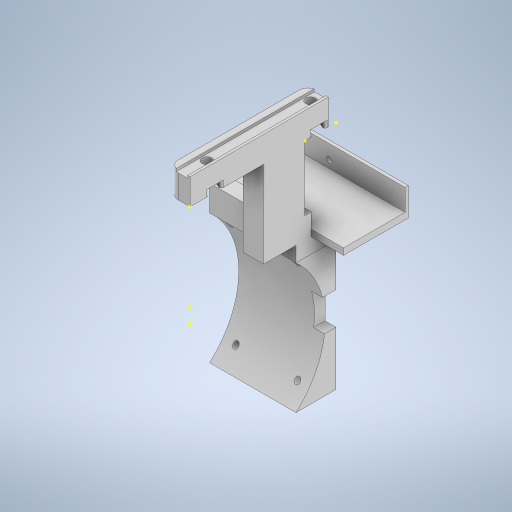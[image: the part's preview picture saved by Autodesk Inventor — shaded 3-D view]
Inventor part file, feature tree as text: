
AUTODESK INVENTOR PART (.ipt)
format: ipt  version: 2024 (Build 280153000, 153)  size: 507,392 bytes
history: native  units: in
note: dims shown in document units (in); Inventor stores cm internally (conversion verified against a paired STEP export)
features: sketch x26, extrude x18, projected_geometry x4, fillet x2, sweep x1
ambient origin geometry x8: Origin, YZ Plane, XZ Plane, XY Plane, X Axis, Y Axis, Z Axis, Center Point
bodies: Solid1 (feature_tree), Solid2 (feature_tree)
feature tree (51):
  extrude  "Extrusion1"  Depth=2.5197in
  extrude  "Extrusion2"  Depth=1.8898in
  extrude  "Extrusion3"  Depth=0.4724in TaperAngle=0.0deg
  fillet  "Fillet1"  Radius=0.0433in
  fillet  "Fillet2"  Radius=0.2126in
  extrude  "Extrusion19"  Depth=0.4724in TaperAngle=0.0deg
  extrude  "Extrusion21"  Depth=0.1181in TaperAngle=0.0deg
  sketch  "Sketch41"  dims[d17=0.1772in d18=0.0394in]
  extrude  "Extrusion22"  Depth=0.0394in
  extrude  "Extrusion25"  Depth=0.4724in
  sweep  "Sweep4"
  extrude  "Extrusion26"  Depth=0.1181in
  sketch  "Sketch60"  dims[d136=0.2756in d137=1.5748in]
  extrude  "Extrusion27"  Depth=0.3937in TaperAngle=0.0deg
  sketch  "Sketch62"  dims[d154=4.1063in d155=0.0in d164=2.3622in]
  extrude  "Extrusion28"  TaperAngle=180.0deg  [1 undecoded]
  sketch  "Sketch64"  dims[d168=2.4813in d169=0.0in d170=1.5748in d171=0.0in]
  extrude  "Extrusion29"  Depth=1.5748in
  sketch  "Sketch66"  dims[d179=0.5906in d180=0.1969in]
  sketch  "Sketch67"  dims[d181=0.5906in d182=0.8248in d183=0.0in]
  extrude  "Extrusion30"  Depth=0.2756in TaperAngle=0.0deg
  extrude  "Extrusion31"  Depth=2.3622in
  extrude  "Extrusion32"  TaperAngle=0.0deg  [1 undecoded]
  extrude  "Extrusion33"  Depth=1.5748in TaperAngle=0.0deg
  extrude  "Extrusion34"  Depth=1.5748in TaperAngle=0.0deg
  extrude  "Extrusion35"  Depth=0.1969in
  extrude  "Extrusion36"  Depth=0.8248in TaperAngle=0.0deg
  sketch  "Sketch1"  dims[d1=0.374in d2=2.5197in]
  sketch  "Sketch2"  dims[d3=0.1772in d4=1.8898in]
  sketch  "Sketch3"  dims[d6=0.1457in d7=0.4724in d8=0.0in d9=0.0433in d10=0.2126in]
  projected_geometry  "Projected Loop2"
  projected_geometry  "Projected Loop3"
  projected_geometry  "Projected Loop4"
  projected_geometry  "Projected Loop5"
  sketch  "Sketch28"  dims[d11=0.0472in d12=0.4724in d13=0.0in]
  sketch  "Sketch40"  dims[d14=0.2953in d15=0.1181in d16=0.0in]
  sketch  "Sketch42"  dims[d19=0.1575in d76=0.4724in]
  sketch  "Sketch54"  dims[d107=0.102in d108=0.748in]
  sketch  "Sketch56"  dims[d109=1.1811in d110=0.0in d130=0.1181in]
  sketch  "Sketch58"  dims[d131=0.8661in d132=0.3937in d133=0.0in]
  sketch  "Sketch59"  dims[d134=1.2008in d135=180.0deg]
  sketch  "Sketch61"  dims[d138=0.2756in d139=0.2756in d140=0.0in]
  sketch  "Sketch63"  dims[d165=1.5748in d166=0.0in d167=0.0in]
  sketch  "Sketch65"  dims[d172=0.2756in d173=1.5748in d174=0.0in]
  sketch  "Sketch68"  dims[d184=0.5906in]
  sketch  "Sketch69"  dims[d187=1.1811in]
  sketch  "Sketch70"  dims[d188=0.1181in d189=0.0in]
  sketch  "Sketch72"  dims[d190=0.1181in d191=0.0in]
  sketch  "Sketch73"  dims[d192=0.0591in]
  sketch  "Sketch74"  dims[d193=0.3937in d194=0.0in]
  sketch  "Sketch75"  dims[d195=0.0394in d196=0.1181in d197=1.4961in d198=2.2047in d199=0.1969in d200=0.1575in d201=0.0984in d202=0.1378in d203=0.1575in d204=0.0984in d205=0.1378in d206=0.1575in d207=0.0984in d208=0.1772in d209=0.1575in d210=0.0984in d211=2.8312in d212=0.0in d213=0.2756in d214=0.0787in d215=1.2008in d216=0.0in d218=0.0984in d219=0.3937in d220=0.0in d221=0.7874in d222=0.0984in d223=0.3937in d224=0.0in d42=0.0197in d43=0.0344in d44=0.0197in d45=0.0344in d46=0.0in d47=0.0in d48=0.0in d49=0.0in d50=0.0in d51=0.0in d52=0.0in d53=0.0in d55=0.0197in d56=0.0344in d57=0.0197in d58=0.0344in d60=0.0197in d61=0.0344in d62=0.0197in d63=0.0344in d72=0.0197in d73=0.0344in d74=0.0197in d75=0.0344in]
note: 2 required parameter values undecoded (feature->parameter linkage not recoverable at this tier; creation-order binding heuristic only, values carry confidence <= 0.55)
